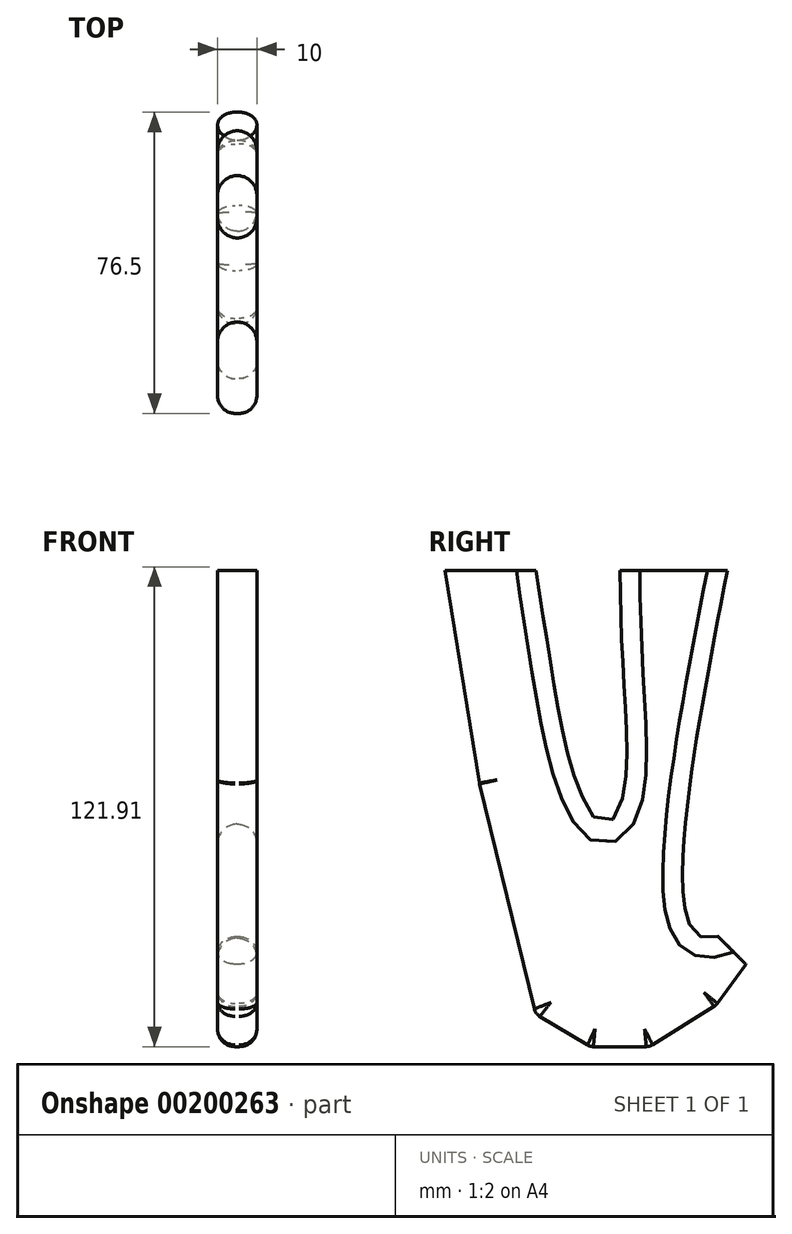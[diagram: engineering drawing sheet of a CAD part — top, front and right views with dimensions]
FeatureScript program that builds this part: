
annotation { "Feature Type Name" : "Feature", "Feature Type Description" : "" }
export const myFeature = defineFeature(function(context is Context, id is Id, definition is map)
    precondition{}
    {
        {
            var Q0;
            Q0=qCreatedBy(makeId("Top.planeOp"),FACE);
            var sketch = newSketch(context, id + "F0", { "sketchPlane" : qUnion([Q0])});
            skLineSegment(sketch, "E0.bottom", {"start": v(50, 50) * mm, "end": v(-50, 50) * mm});
            skLineSegment(sketch, "E0.top", {"start": v(50, -50) * mm, "end": v(-50, -50) * mm});
            skLineSegment(sketch, "E0.left", {"start": v(50, 50) * mm, "end": v(50, -50) * mm});
            skLineSegment(sketch, "E0.right", {"start": v(-50, 50) * mm, "end": v(-50, -50) * mm});
            skPoint(sketch, "E0.middle", {"position": v(0, 0) * mm});
            skSolve(sketch);
        }
        {
            var Q0;
            Q0=qCreatedBy(makeId("Right.planeOp"),FACE);
            var sketch = newSketch(context, id + "F1", { "sketchPlane" : qUnion([Q0])});
            skLineSegment(sketch, "E1", {"start": v(32.93, -92.93) * mm, "end": v(40, -100) * mm});
            skLineSegment(sketch, "E2", {"start": v(40, -100) * mm, "end": v(50, -100) * mm});
            skLineSegment(sketch, "E3", {"start": v(50, -100) * mm, "end": v(50, 0) * mm});
            skLineSegment(sketch, "E4", {"start": v(40, -100) * mm, "end": v(32.42, -110.44) * mm});
            skLineSegment(sketch, "E5", {"start": v(32.42, -110.44) * mm, "end": v(15.56, -120.94) * mm});
            skLineSegment(sketch, "E6", {"start": v(15.56, -120.94) * mm, "end": v(0.42, -120.94) * mm});
            skLineSegment(sketch, "E7", {"start": v(0.42, -120.94) * mm, "end": v(-13.45, -112.58) * mm});
            skLineSegment(sketch, "E8", {"start": v(-13.45, -112.58) * mm, "end": v(-27.68, -54.06) * mm});
            skLineSegment(sketch, "E9", {"start": v(-27.68, -54.06) * mm, "end": v(-36.5, 0) * mm});
            skFitSpline(sketch, "E10", {"points": [v(32.93, -92.93) * mm, v(25.29, -88.96) * mm, v(35.31, 0) * mm], "startDerivative": vector(-48.83, -14.77) * mm, "endDerivative": vector(30.46, 154.64) * mm});
            skFitSpline(sketch, "E11", {"points": [v(8.07, 0) * mm, v(8.9, -56.9) * mm, v(4.16, -64.38) * mm, v(-2.6, -54.96) * mm, v(-13.28, 0) * mm], "startDerivative": vector(0.01, -244.79) * mm, "endDerivative": vector(-35.2, 225.8) * mm});
            skLineSegment(sketch, "E12", {"start": v(35.31, 0) * mm, "end": v(8.07, 0) * mm});
            skLineSegment(sketch, "E13", {"start": v(-13.28, 0) * mm, "end": v(-36.5, 0) * mm});
            skSolve(sketch);
        }
        {
            var Q0;
            Q0=sQuery(id+"F1.wireOp",EDGE,"E1");
            extrude(context, id + "F2", {"bodyType" : ToolBodyType.SURFACE, "surfaceEntities" : qUnion([Q0]), "endBound" : BoundingType.SYMMETRIC, "depth" : 10 * mm});
        }
        {
            var Q0;
            Q0=qSketchRegion(id+"F1",true);
            extrude(context, id + "F3", {"entities" : qUnion([Q0]), "endBound" : BoundingType.SYMMETRIC, "depth" : 10 * mm});
        }
        {
            var Q0;
            Q0=makeQuery(id+"F3.opExtrude","CAP_EDGE",EDGE,{"disambiguationData":[OSD([sQuery(id+"F1.wireOp",EDGE,"6j2MmI0v-9CaA-rXXN-4GS7-BZTnkRh6syKU")])],"isStart":false});
            var Q1;
            Q1=makeQuery(id+"F3.opExtrude","CAP_EDGE",EDGE,{"disambiguationData":[OSD([sQuery(id+"F1.wireOp",EDGE,"E4")])],"isStart":false});
            var Q2;
            Q2=makeQuery(id+"F3.opExtrude","CAP_EDGE",EDGE,{"disambiguationData":[OSD([sQuery(id+"F1.wireOp",EDGE,"E4")])],"isStart":true});
            var Q3;
            Q3=makeQuery(id+"F3.opExtrude","CAP_EDGE",EDGE,{"disambiguationData":[OSD([sQuery(id+"F1.wireOp",EDGE,"6j2MmI0v-9CaA-rXXN-4GS7-BZTnkRh6syKU")])],"isStart":true});
            var Q4;
            Q4=makeQuery(id+"F3.opExtrude","CAP_EDGE",EDGE,{"disambiguationData":[OSD([sQuery(id+"F1.wireOp",EDGE,"1lMwgCfK-8zYP-9geR-T3N1-000Z4BXpfQfB")])],"isStart":false});
            var Q5;
            Q5=makeQuery(id+"F3.opExtrude","CAP_EDGE",EDGE,{"disambiguationData":[OSD([sQuery(id+"F1.wireOp",EDGE,"1lMwgCfK-8zYP-9geR-T3N1-000Z4BXpfQfB")])],"isStart":true});
            var Q6;
            Q6=makeQuery(id+"F3.opExtrude","CAP_EDGE",EDGE,{"disambiguationData":[OSD([sQuery(id+"F1.wireOp",EDGE,"E5")])],"isStart":false});
            var Q7;
            Q7=makeQuery(id+"F3.opExtrude","CAP_EDGE",EDGE,{"disambiguationData":[OSD([sQuery(id+"F1.wireOp",EDGE,"E5")])],"isStart":true});
            var Q8;
            Q8=makeQuery(id+"F3.opExtrude","CAP_EDGE",EDGE,{"disambiguationData":[OSD([sQuery(id+"F1.wireOp",EDGE,"E6")])],"isStart":true});
            var Q9;
            Q9=makeQuery(id+"F3.opExtrude","CAP_EDGE",EDGE,{"disambiguationData":[OSD([sQuery(id+"F1.wireOp",EDGE,"E6")])],"isStart":false});
            var Q10;
            Q10=makeQuery(id+"F3.opExtrude","CAP_EDGE",EDGE,{"disambiguationData":[OSD([sQuery(id+"F1.wireOp",EDGE,"E7")])],"isStart":false});
            var Q11;
            Q11=makeQuery(id+"F3.opExtrude","CAP_EDGE",EDGE,{"disambiguationData":[OSD([sQuery(id+"F1.wireOp",EDGE,"E7")])],"isStart":true});
            var Q12;
            Q12=makeQuery(id+"F3.opExtrude","CAP_EDGE",EDGE,{"disambiguationData":[OSD([sQuery(id+"F1.wireOp",EDGE,"E8")])],"isStart":true});
            var Q13;
            Q13=makeQuery(id+"F3.opExtrude","CAP_EDGE",EDGE,{"disambiguationData":[OSD([sQuery(id+"F1.wireOp",EDGE,"E9")])],"isStart":true});
            var Q14;
            Q14=makeQuery(id+"F3.opExtrude","CAP_EDGE",EDGE,{"disambiguationData":[OSD([sQuery(id+"F1.wireOp",EDGE,"E8")])],"isStart":false});
            var Q15;
            Q15=makeQuery(id+"F3.opExtrude","CAP_EDGE",EDGE,{"disambiguationData":[OSD([sQuery(id+"F1.wireOp",EDGE,"E9")])],"isStart":false});
            var Q16;
            Q16=makeQuery(id+"F3.opExtrude","CAP_EDGE",EDGE,{"disambiguationData":[OSD([sQuery(id+"F1.wireOp",EDGE,"PjlUZDiv-9Nuz-91em-e2Fd-0O4rsgYu6psd")])],"isStart":false});
            var Q17;
            Q17=makeQuery(id+"F3.opExtrude","CAP_EDGE",EDGE,{"disambiguationData":[OSD([sQuery(id+"F1.wireOp",EDGE,"PjlUZDiv-9Nuz-91em-e2Fd-0O4rsgYu6psd")])],"isStart":true});
            var Q18;
            Q18=makeQuery(id+"F3.opExtrude","CAP_EDGE",EDGE,{"disambiguationData":[OSD([sQuery(id+"F1.wireOp",EDGE,"ZAGma3XW-A2qp-hiio-JgDo-AlgzH9WFpZtm")])],"isStart":false});
            var Q19;
            Q19=makeQuery(id+"F3.opExtrude","CAP_EDGE",EDGE,{"disambiguationData":[OSD([sQuery(id+"F1.wireOp",EDGE,"ZAGma3XW-A2qp-hiio-JgDo-AlgzH9WFpZtm")])],"isStart":true});
            fillet(context, id + "F4", {"entities" : qUnion([Q0, Q1, Q2, Q3, Q4, Q5, Q6, Q7, Q8, Q9, Q10, Q11, Q12, Q13, Q14, Q15, Q16, Q17, Q18, Q19]), "radius" : 4.5 * mm, "tangentPropagation" : true, "allowEdgeOverflow" : false});
        }
        {
            var Q0;
            Q0=makeQuery(id+"F4.opFillet","BLEND_EDGE",EDGE,{"blendedFrom":[makeQuery(id+"F3.opExtrude","CAP_EDGE",EDGE,{"disambiguationData":[OSD([sQuery(id+"F1.wireOp",EDGE,"1lMwgCfK-8zYP-9geR-T3N1-000Z4BXpfQfB")])],"isStart":false}),makeQuery(id+"F3.opExtrude","CAP_EDGE",EDGE,{"disambiguationData":[OSD([sQuery(id+"F1.wireOp",EDGE,"PjlUZDiv-9Nuz-91em-e2Fd-0O4rsgYu6psd")])],"isStart":false})],"blendedInto":[]});
            var Q1;
            Q1=makeQuery(id+"F4.opFillet","BLEND_EDGE",EDGE,{"blendedFrom":[makeQuery(id+"F3.opExtrude","CAP_EDGE",EDGE,{"disambiguationData":[OSD([sQuery(id+"F1.wireOp",EDGE,"1lMwgCfK-8zYP-9geR-T3N1-000Z4BXpfQfB")])],"isStart":true}),makeQuery(id+"F3.opExtrude","CAP_EDGE",EDGE,{"disambiguationData":[OSD([sQuery(id+"F1.wireOp",EDGE,"PjlUZDiv-9Nuz-91em-e2Fd-0O4rsgYu6psd")])],"isStart":true})],"blendedInto":[]});
            var Q2;
            Q2=makeQuery(id+"F4.opFillet","BLEND_EDGE",EDGE,{"blendedFrom":[makeQuery(id+"F3.opExtrude","CAP_EDGE",EDGE,{"disambiguationData":[OSD([sQuery(id+"F1.wireOp",EDGE,"6j2MmI0v-9CaA-rXXN-4GS7-BZTnkRh6syKU")])],"isStart":false}),makeQuery(id+"F3.opExtrude","CAP_EDGE",EDGE,{"disambiguationData":[OSD([sQuery(id+"F1.wireOp",EDGE,"1lMwgCfK-8zYP-9geR-T3N1-000Z4BXpfQfB")])],"isStart":false})],"blendedInto":[]});
            var Q3;
            Q3=makeQuery(id+"F4.opFillet","BLEND_EDGE",EDGE,{"blendedFrom":[makeQuery(id+"F3.opExtrude","CAP_EDGE",EDGE,{"disambiguationData":[OSD([sQuery(id+"F1.wireOp",EDGE,"6j2MmI0v-9CaA-rXXN-4GS7-BZTnkRh6syKU")])],"isStart":true}),makeQuery(id+"F3.opExtrude","CAP_EDGE",EDGE,{"disambiguationData":[OSD([sQuery(id+"F1.wireOp",EDGE,"1lMwgCfK-8zYP-9geR-T3N1-000Z4BXpfQfB")])],"isStart":true})],"blendedInto":[]});
            var Q4;
            Q4=makeQuery(id+"F4.opFillet","BLEND_EDGE",EDGE,{"blendedFrom":[makeQuery(id+"F3.opExtrude","CAP_EDGE",EDGE,{"disambiguationData":[OSD([sQuery(id+"F1.wireOp",EDGE,"PjlUZDiv-9Nuz-91em-e2Fd-0O4rsgYu6psd")])],"isStart":false}),makeQuery(id+"F3.opExtrude","CAP_EDGE",EDGE,{"disambiguationData":[OSD([sQuery(id+"F1.wireOp",EDGE,"ZAGma3XW-A2qp-hiio-JgDo-AlgzH9WFpZtm")])],"isStart":false})],"blendedInto":[]});
            var Q5;
            Q5=makeQuery(id+"F4.opFillet","BLEND_EDGE",EDGE,{"blendedFrom":[makeQuery(id+"F3.opExtrude","CAP_EDGE",EDGE,{"disambiguationData":[OSD([sQuery(id+"F1.wireOp",EDGE,"PjlUZDiv-9Nuz-91em-e2Fd-0O4rsgYu6psd")])],"isStart":true}),makeQuery(id+"F3.opExtrude","CAP_EDGE",EDGE,{"disambiguationData":[OSD([sQuery(id+"F1.wireOp",EDGE,"ZAGma3XW-A2qp-hiio-JgDo-AlgzH9WFpZtm")])],"isStart":true})],"blendedInto":[]});
            var Q6;
            Q6=makeQuery(id+"F4.opFillet","BLEND_EDGE",EDGE,{"blendedFrom":[makeQuery(id+"F3.opExtrude","CAP_EDGE",EDGE,{"disambiguationData":[OSD([sQuery(id+"F1.wireOp",EDGE,"E4")])],"isStart":true}),makeQuery(id+"F3.opExtrude","CAP_EDGE",EDGE,{"disambiguationData":[OSD([sQuery(id+"F1.wireOp",EDGE,"E5")])],"isStart":true})],"blendedInto":[]});
            var Q7;
            Q7=makeQuery(id+"F4.opFillet","BLEND_EDGE",EDGE,{"blendedFrom":[makeQuery(id+"F3.opExtrude","CAP_EDGE",EDGE,{"disambiguationData":[OSD([sQuery(id+"F1.wireOp",EDGE,"E4")])],"isStart":false}),makeQuery(id+"F3.opExtrude","CAP_EDGE",EDGE,{"disambiguationData":[OSD([sQuery(id+"F1.wireOp",EDGE,"E5")])],"isStart":false})],"blendedInto":[]});
            var Q8;
            Q8=makeQuery(id+"F4.opFillet","BLEND_EDGE",EDGE,{"blendedFrom":[makeQuery(id+"F3.opExtrude","CAP_EDGE",EDGE,{"disambiguationData":[OSD([sQuery(id+"F1.wireOp",EDGE,"E5")])],"isStart":true}),makeQuery(id+"F3.opExtrude","CAP_EDGE",EDGE,{"disambiguationData":[OSD([sQuery(id+"F1.wireOp",EDGE,"E6")])],"isStart":true})],"blendedInto":[]});
            var Q9;
            Q9=makeQuery(id+"F4.opFillet","BLEND_EDGE",EDGE,{"blendedFrom":[makeQuery(id+"F3.opExtrude","CAP_EDGE",EDGE,{"disambiguationData":[OSD([sQuery(id+"F1.wireOp",EDGE,"E5")])],"isStart":false}),makeQuery(id+"F3.opExtrude","CAP_EDGE",EDGE,{"disambiguationData":[OSD([sQuery(id+"F1.wireOp",EDGE,"E6")])],"isStart":false})],"blendedInto":[]});
            var Q10;
            Q10=makeQuery(id+"F4.opFillet","BLEND_EDGE",EDGE,{"blendedFrom":[makeQuery(id+"F3.opExtrude","CAP_EDGE",EDGE,{"disambiguationData":[OSD([sQuery(id+"F1.wireOp",EDGE,"E6")])],"isStart":false}),makeQuery(id+"F3.opExtrude","CAP_EDGE",EDGE,{"disambiguationData":[OSD([sQuery(id+"F1.wireOp",EDGE,"E7")])],"isStart":false})],"blendedInto":[]});
            var Q11;
            Q11=makeQuery(id+"F4.opFillet","BLEND_EDGE",EDGE,{"blendedFrom":[makeQuery(id+"F3.opExtrude","CAP_EDGE",EDGE,{"disambiguationData":[OSD([sQuery(id+"F1.wireOp",EDGE,"E6")])],"isStart":true}),makeQuery(id+"F3.opExtrude","CAP_EDGE",EDGE,{"disambiguationData":[OSD([sQuery(id+"F1.wireOp",EDGE,"E7")])],"isStart":true})],"blendedInto":[]});
            var Q12;
            Q12=makeQuery(id+"F4.opFillet","BLEND_EDGE",EDGE,{"blendedFrom":[makeQuery(id+"F3.opExtrude","CAP_EDGE",EDGE,{"disambiguationData":[OSD([sQuery(id+"F1.wireOp",EDGE,"E7")])],"isStart":true}),makeQuery(id+"F3.opExtrude","CAP_EDGE",EDGE,{"disambiguationData":[OSD([sQuery(id+"F1.wireOp",EDGE,"E8")])],"isStart":true})],"blendedInto":[]});
            var Q13;
            Q13=makeQuery(id+"F4.opFillet","BLEND_EDGE",EDGE,{"blendedFrom":[makeQuery(id+"F3.opExtrude","CAP_EDGE",EDGE,{"disambiguationData":[OSD([sQuery(id+"F1.wireOp",EDGE,"E7")])],"isStart":false}),makeQuery(id+"F3.opExtrude","CAP_EDGE",EDGE,{"disambiguationData":[OSD([sQuery(id+"F1.wireOp",EDGE,"E8")])],"isStart":false})],"blendedInto":[]});
            var Q14;
            Q14=makeQuery(id+"F4.opFillet","BLEND_EDGE",EDGE,{"blendedFrom":[makeQuery(id+"F3.opExtrude","CAP_EDGE",EDGE,{"disambiguationData":[OSD([sQuery(id+"F1.wireOp",EDGE,"E8")])],"isStart":true}),makeQuery(id+"F3.opExtrude","CAP_EDGE",EDGE,{"disambiguationData":[OSD([sQuery(id+"F1.wireOp",EDGE,"E9")])],"isStart":true})],"blendedInto":[]});
            var Q15;
            Q15=makeQuery(id+"F4.opFillet","BLEND_EDGE",EDGE,{"blendedFrom":[makeQuery(id+"F3.opExtrude","CAP_EDGE",EDGE,{"disambiguationData":[OSD([sQuery(id+"F1.wireOp",EDGE,"E8")])],"isStart":false}),makeQuery(id+"F3.opExtrude","CAP_EDGE",EDGE,{"disambiguationData":[OSD([sQuery(id+"F1.wireOp",EDGE,"E9")])],"isStart":false})],"blendedInto":[]});
            fillet(context, id + "F5", {"entities" : qUnion([Q0, Q1, Q2, Q3, Q4, Q5, Q6, Q7, Q8, Q9, Q10, Q11, Q12, Q13, Q14, Q15]), "radius" : 3 * mm, "tangentPropagation" : true, "allowEdgeOverflow" : false});
        }
        {
            var Q0;
            Q0=makeQuery(id+"F3.opExtrude","CAP_EDGE",EDGE,{"disambiguationData":[OSD([sQuery(id+"F1.wireOp",EDGE,"E10")])],"isStart":false});
            var Q1;
            Q1=makeQuery(id+"F3.opExtrude","CAP_EDGE",EDGE,{"disambiguationData":[OSD([sQuery(id+"F1.wireOp",EDGE,"E10")])],"isStart":true});
            var Q2;
            Q2=makeQuery(id+"F3.opExtrude","CAP_EDGE",EDGE,{"disambiguationData":[OSD([sQuery(id+"F1.wireOp",EDGE,"E11")])],"isStart":false});
            var Q3;
            Q3=makeQuery(id+"F3.opExtrude","CAP_EDGE",EDGE,{"disambiguationData":[OSD([sQuery(id+"F1.wireOp",EDGE,"E11")])],"isStart":true});
            fillet(context, id + "F6", {"entities" : qUnion([Q0, Q1, Q2, Q3]), "radius" : 5 * mm, "tangentPropagation" : true, "allowEdgeOverflow" : false});
        }
    });
